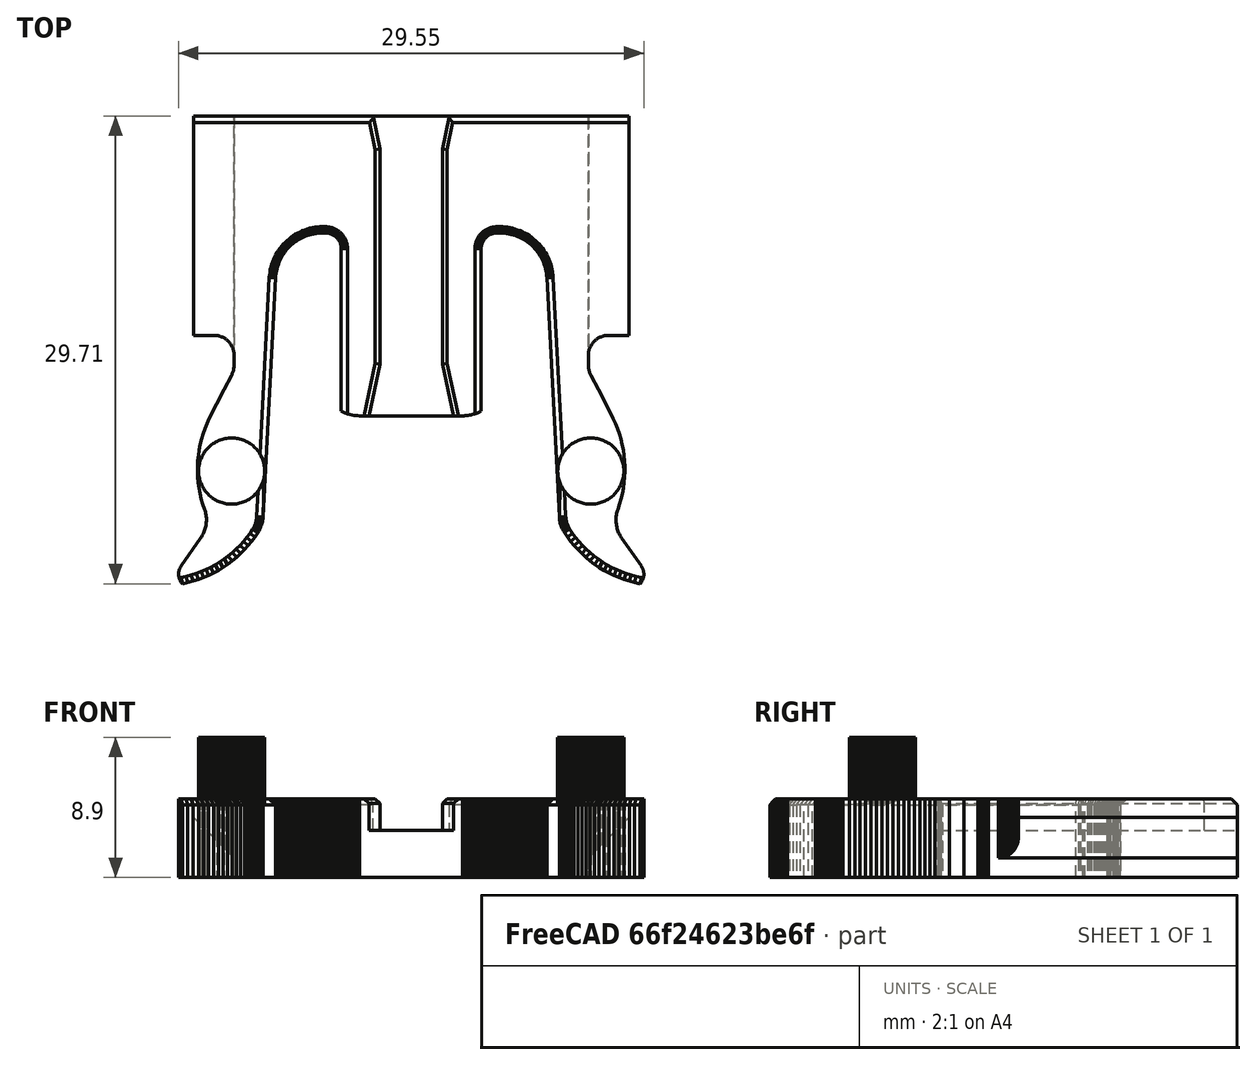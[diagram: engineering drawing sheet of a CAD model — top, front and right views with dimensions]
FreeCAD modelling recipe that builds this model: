
FCSTD DOCUMENT  (FreeCAD 0.22R36534 (Git))
Label: kusba quick release
License: All rights reserved
LicenseURL: http://en.wikipedia.org/wiki/All_rights_reserved
objects: Part::Feature×1, PartDesign::FeatureBase×1, Sketcher::SketchObject×1, PartDesign::Body×1
note: 4 computed .brp shape members not serialized (recipe doc carries the construction recipe); baked Part::Feature solids carry a one-line shape summary decoded from their .brp

FEATURE [Part::Feature] kusba_quick_release_Body
  shape: bbox 29.55 x 29.71 x 8.9 mm, 1639 faces (baked)
FEATURE [PartDesign::FeatureBase] BaseFeature
  BaseFeature = -> kusba_quick_release_Body
  Suppressed = false
FEATURE [Sketcher::SketchObject] Sketch
  AttachmentSupport = -> [BaseFeature]
  ExternalGeometry = -> [BaseFeature]
  FullyConstrained = true
  MapMode = 5
  Placement = pos=(0,0,15.5325) rot=(0,0,1;0rad)
  sketch-geometry (5):
    g0: Circle CenterX=126.404 CenterY=61.6594 CenterZ=0 NormalX=0 NormalY=0 NormalZ=1 AngleXU=0 Radius=1.5
    g1: Circle CenterX=149.904 CenterY=61.6594 CenterZ=0 NormalX=0 NormalY=0 NormalZ=1 AngleXU=0 Radius=1.5
    g2: GeomPoint X=138.154 Y=61.6594 Z=0
    g3: GeomPoint X=124.334 Y=61.6594 Z=0
    g4: GeomPoint X=151.974 Y=61.6594 Z=0
  constraints (10):
    c: Equal(g1,g0)
    c: Horizontal(g1,g0)
    c: Diameter(g0) = 3
    c: Symmetric(g0,g1,g2)
    c: DistanceY(g0,g-3) = 3
    c: PointOnObject(g3,g-3)
    c: PointOnObject(g4,g-4)
    c: Horizontal(g3,g0)
    c: Symmetric(g3,g4,g2)
    c: DistanceX(g0,g1) = 23.5
FEATURE [PartDesign::Body] Body
  BaseFeature = -> kusba_quick_release_Body
  Group = -> [BaseFeature,Sketch]
  Origin = -> Origin
  Tip = -> BaseFeature
